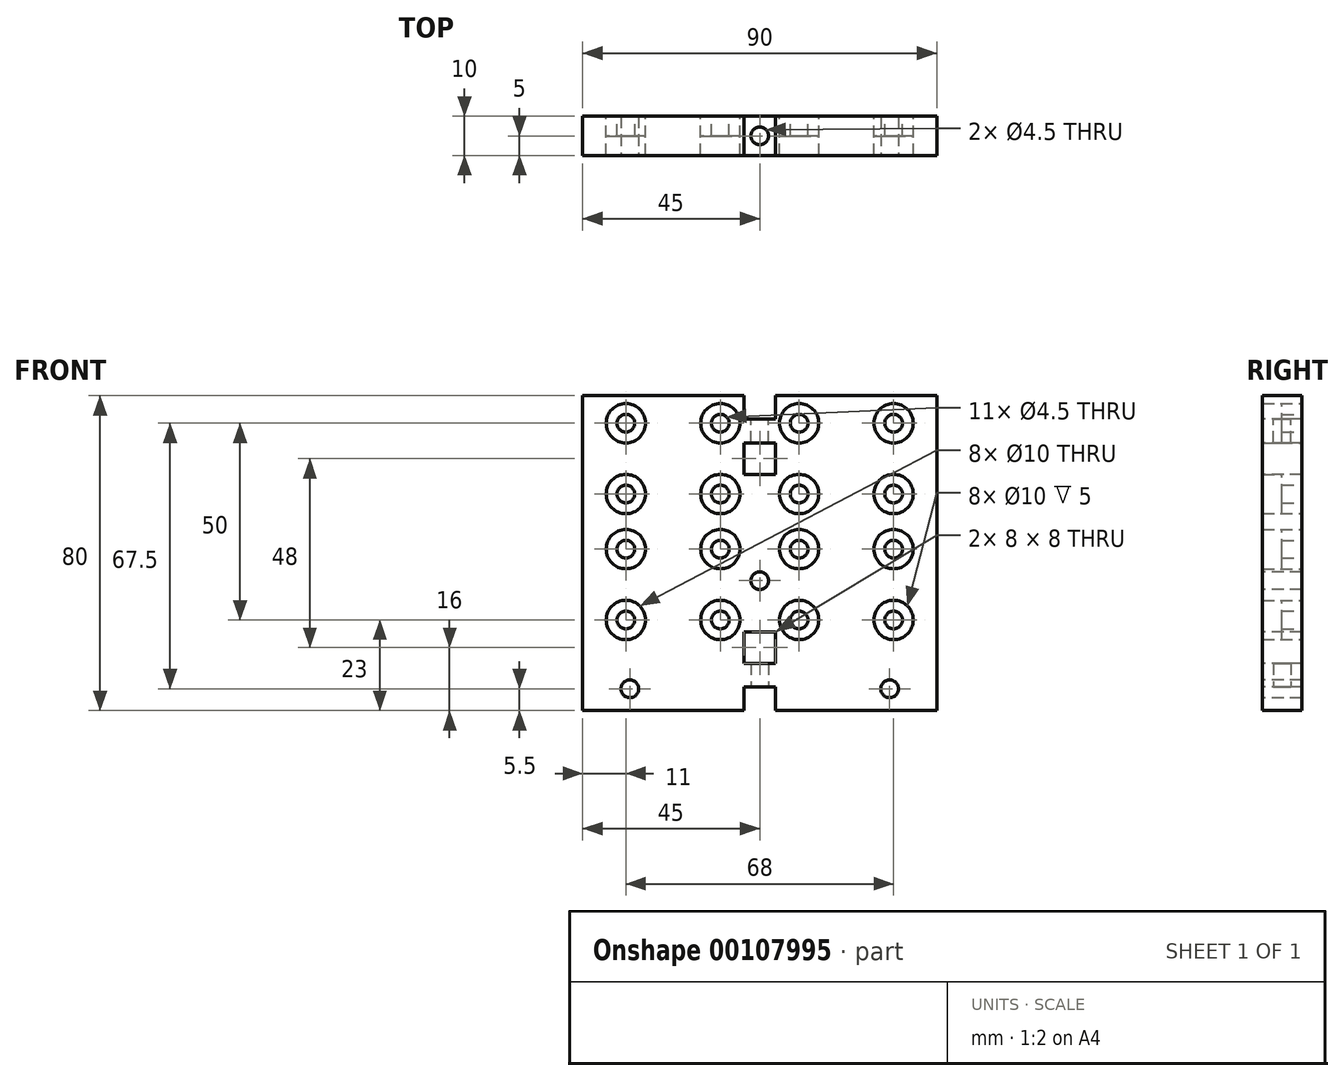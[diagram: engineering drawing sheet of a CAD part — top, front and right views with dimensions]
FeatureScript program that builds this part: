
annotation { "Feature Type Name" : "Feature", "Feature Type Description" : "" }
export const myFeature = defineFeature(function(context is Context, id is Id, definition is map)
    precondition{}
    {
        {
            var Q0;
            Q0=qCreatedBy(makeId("Front.planeOp"),FACE);
            var sketch = newSketch(context, id + "F0", { "sketchPlane" : qUnion([Q0])});
            skLineSegment(sketch, "E0.bottom", {"start": v(0, 0) * mm, "end": v(90, 0) * mm});
            skLineSegment(sketch, "E0.top", {"start": v(0, 80) * mm, "end": v(90, 80) * mm});
            skLineSegment(sketch, "E0.left", {"start": v(0, 0) * mm, "end": v(0, 80) * mm});
            skLineSegment(sketch, "E0.right", {"start": v(90, 0) * mm, "end": v(90, 80) * mm});
            skLineSegment(sketch, "E1.bottom", {"start": v(6, 79) * mm, "end": v(40, 79) * mm});
            skLineSegment(sketch, "E1.top", {"start": v(6, 49) * mm, "end": v(40, 49) * mm});
            skLineSegment(sketch, "E1.left", {"start": v(6, 79) * mm, "end": v(6, 49) * mm});
            skLineSegment(sketch, "E1.right", {"start": v(40, 79) * mm, "end": v(40, 49) * mm});
            skLineSegment(sketch, "E2", {"start": v(45, 80) * mm, "end": v(45, 0) * mm, "construction": true});
            skLineSegment(sketch, "E3", {"start": v(0, 48) * mm, "end": v(90, 48) * mm, "construction": true});
            skCircle(sketch, "E4", {"center": v(11, 73) * mm, "radius": 2.25 * mm});
            skCircle(sketch, "E5", {"center": v(35, 73) * mm, "radius": 2.25 * mm});
            skCircle(sketch, "E6", {"center": v(35, 55) * mm, "radius": 2.25 * mm});
            skCircle(sketch, "E7", {"center": v(11, 55) * mm, "radius": 2.25 * mm});
            skCircle(sketch, "E8.MirrorC", {"center": v(55, 55) * mm, "radius": 2.25 * mm});
            skCircle(sketch, "E9.MirrorC", {"center": v(55, 73) * mm, "radius": 2.25 * mm});
            skCircle(sketch, "E10.MirrorC", {"center": v(79, 55) * mm, "radius": 2.25 * mm});
            skCircle(sketch, "E11.MirrorC", {"center": v(79, 73) * mm, "radius": 2.25 * mm});
            skLineSegment(sketch, "E12.MirrorCS", {"start": v(84, 49) * mm, "end": v(50, 49) * mm});
            skLineSegment(sketch, "E13.MirrorCS", {"start": v(84, 79) * mm, "end": v(50, 79) * mm});
            skLineSegment(sketch, "E14.MirrorCS", {"start": v(84, 79) * mm, "end": v(84, 49) * mm});
            skLineSegment(sketch, "E15.MirrorCS", {"start": v(50, 79) * mm, "end": v(50, 49) * mm});
            skLineSegment(sketch, "E16.MirrorCS", {"start": v(84, 17) * mm, "end": v(84, 47) * mm});
            skLineSegment(sketch, "E17.MirrorCS", {"start": v(84, 47) * mm, "end": v(50, 47) * mm});
            skLineSegment(sketch, "E18.MirrorCS", {"start": v(84, 17) * mm, "end": v(50, 17) * mm});
            skCircle(sketch, "E19.MirrorC", {"center": v(79, 41) * mm, "radius": 2.25 * mm});
            skCircle(sketch, "E20.MirrorC", {"center": v(79, 23) * mm, "radius": 2.25 * mm});
            skCircle(sketch, "E21.MirrorC", {"center": v(55, 23) * mm, "radius": 2.25 * mm});
            skLineSegment(sketch, "E22.MirrorCS", {"start": v(50, 17) * mm, "end": v(50, 47) * mm});
            skCircle(sketch, "E23.MirrorC", {"center": v(55, 41) * mm, "radius": 2.25 * mm});
            skCircle(sketch, "E24.MirrorC", {"center": v(11, 23) * mm, "radius": 2.25 * mm});
            skLineSegment(sketch, "E25.MirrorCS", {"start": v(40, 17) * mm, "end": v(40, 47) * mm});
            skCircle(sketch, "E26.MirrorC", {"center": v(35, 23) * mm, "radius": 2.25 * mm});
            skCircle(sketch, "E27.MirrorC", {"center": v(35, 41) * mm, "radius": 2.25 * mm});
            skLineSegment(sketch, "E28.MirrorCS", {"start": v(6, 17) * mm, "end": v(40, 17) * mm});
            skLineSegment(sketch, "E29.MirrorCS", {"start": v(6, 47) * mm, "end": v(40, 47) * mm});
            skLineSegment(sketch, "E30.MirrorCS", {"start": v(6, 17) * mm, "end": v(6, 47) * mm});
            skCircle(sketch, "E31.MirrorC", {"center": v(11, 41) * mm, "radius": 2.25 * mm});
            skCircle(sketch, "E32", {"center": v(11, 73) * mm, "radius": 5 * mm});
            skCircle(sketch, "E33", {"center": v(11, 55) * mm, "radius": 5 * mm});
            skCircle(sketch, "E34", {"center": v(35, 55) * mm, "radius": 5 * mm});
            skCircle(sketch, "E35", {"center": v(35, 73) * mm, "radius": 5 * mm});
            skCircle(sketch, "E36", {"center": v(55, 73) * mm, "radius": 5 * mm});
            skCircle(sketch, "E37", {"center": v(55, 55) * mm, "radius": 5 * mm});
            skCircle(sketch, "E38", {"center": v(79, 73) * mm, "radius": 5 * mm});
            skCircle(sketch, "E39", {"center": v(79, 55) * mm, "radius": 5 * mm});
            skCircle(sketch, "E40", {"center": v(79, 41) * mm, "radius": 5 * mm});
            skCircle(sketch, "E41", {"center": v(55, 41) * mm, "radius": 5 * mm});
            skCircle(sketch, "E42", {"center": v(35, 41) * mm, "radius": 5 * mm});
            skCircle(sketch, "E43", {"center": v(11, 41) * mm, "radius": 5 * mm});
            skCircle(sketch, "E44", {"center": v(35, 23) * mm, "radius": 5 * mm});
            skCircle(sketch, "E45", {"center": v(11, 23) * mm, "radius": 5 * mm});
            skCircle(sketch, "E46", {"center": v(55, 23) * mm, "radius": 5 * mm});
            skCircle(sketch, "E47", {"center": v(79, 23) * mm, "radius": 5 * mm});
            skSolve(sketch);
        }
        {
            var Q0;
            Q0 = qSketchRegion(id + "F0", true);
            var Q1;
            Q1=makeQuery(id+"F0.imprint","IMPRINT",FACE,{"disambiguationData":[TD([[makeQuery(id+"F0.imprint","IMPRINT",EDGE,{"derivedFrom":sQuery(id+"F0.wireOp",EDGE,"E1.bottom")}),-1.0]])]});
            var Q2;
            Q2=makeQuery(id+"F0.imprint","IMPRINT",FACE,{"disambiguationData":[TD([[makeQuery(id+"F0.imprint","IMPRINT",EDGE,{"derivedFrom":sQuery(id+"F0.wireOp",EDGE,"bZuI6SaU-zsjN-Xk2B-mhtP-13RFlTSP3aNL.bottom")}),-1.0]])]});
            var Q3;
            Q3=makeQuery(id+"F0.imprint","IMPRINT",FACE,{"disambiguationData":[TD([[makeQuery(id+"F0.imprint","IMPRINT",EDGE,{"derivedFrom":sQuery(id+"F0.wireOp",EDGE,"s5ukpUkq-3LvQ-wobc-wGG7-4HGfYjanBSKT.bottom")}),-1.0]])]});
            var Q4;
            Q4=makeQuery(id+"F0.imprint","IMPRINT",FACE,{"disambiguationData":[TD([[makeQuery(id+"F0.imprint","IMPRINT",EDGE,{"derivedFrom":sQuery(id+"F0.wireOp",EDGE,"Jf4Y0yrR-lJhz-zIhG-2X3j-dwFTrGFaGGee.bottom")}),-1.0]])]});
            var Q5;
            Q5=makeQuery(id+"F0.imprint","IMPRINT",FACE,{"disambiguationData":[TD([[makeQuery(id+"F0.imprint","IMPRINT",EDGE,{"derivedFrom":sQuery(id+"F0.wireOp",EDGE,"E12.MirrorCS")}),-1.0]])]});
            var Q6;
            Q6=makeQuery(id+"F0.imprint","IMPRINT",FACE,{"disambiguationData":[TD([[makeQuery(id+"F0.imprint","IMPRINT",EDGE,{"derivedFrom":sQuery(id+"F0.wireOp",EDGE,"E19.MirrorC")}),-1.0]])]});
            var Q7;
            Q7=makeQuery(id+"F0.imprint","IMPRINT",FACE,{"disambiguationData":[TD([[makeQuery(id+"F0.imprint","IMPRINT",EDGE,{"derivedFrom":sQuery(id+"F0.wireOp",EDGE,"E24.MirrorC")}),1.0]])]});
            var Q8;
            Q8=makeQuery(id+"F0.imprint","IMPRINT",FACE,{"disambiguationData":[TD([[makeQuery(id+"F0.imprint","IMPRINT",EDGE,{"derivedFrom":sQuery(id+"F0.wireOp",EDGE,"E4")}),-1.0]])]});
            var Q9;
            Q9=makeQuery(id+"F0.imprint","IMPRINT",FACE,{"disambiguationData":[TD([[makeQuery(id+"F0.imprint","IMPRINT",EDGE,{"derivedFrom":sQuery(id+"F0.wireOp",EDGE,"E5")}),-1.0]])]});
            var Q10;
            Q10=makeQuery(id+"F0.imprint","IMPRINT",FACE,{"disambiguationData":[TD([[makeQuery(id+"F0.imprint","IMPRINT",EDGE,{"derivedFrom":sQuery(id+"F0.wireOp",EDGE,"E9.MirrorC")}),1.0]])]});
            var Q11;
            Q11=makeQuery(id+"F0.imprint","IMPRINT",FACE,{"disambiguationData":[TD([[makeQuery(id+"F0.imprint","IMPRINT",EDGE,{"derivedFrom":sQuery(id+"F0.wireOp",EDGE,"E11.MirrorC")}),1.0]])]});
            var Q12;
            Q12=makeQuery(id+"F0.imprint","IMPRINT",FACE,{"disambiguationData":[TD([[makeQuery(id+"F0.imprint","IMPRINT",EDGE,{"derivedFrom":sQuery(id+"F0.wireOp",EDGE,"E10.MirrorC")}),1.0]])]});
            var Q13;
            Q13=makeQuery(id+"F0.imprint","IMPRINT",FACE,{"disambiguationData":[TD([[makeQuery(id+"F0.imprint","IMPRINT",EDGE,{"derivedFrom":sQuery(id+"F0.wireOp",EDGE,"E8.MirrorC")}),1.0]])]});
            var Q14;
            Q14=makeQuery(id+"F0.imprint","IMPRINT",FACE,{"disambiguationData":[TD([[makeQuery(id+"F0.imprint","IMPRINT",EDGE,{"derivedFrom":sQuery(id+"F0.wireOp",EDGE,"E6")}),-1.0]])]});
            var Q15;
            Q15=makeQuery(id+"F0.imprint","IMPRINT",FACE,{"disambiguationData":[TD([[makeQuery(id+"F0.imprint","IMPRINT",EDGE,{"derivedFrom":sQuery(id+"F0.wireOp",EDGE,"E7")}),-1.0]])]});
            var Q16;
            {var subQ11=sQuery(id+"F0.wireOp",EDGE,"E28.MirrorCS");Q16=makeQuery(id+"F0.imprint","IMPRINT",FACE,{"disambiguationData":[TD([[makeQuery(id+"F0.imprint","IMPRINT",EDGE,{"derivedFrom":subQ11}),1.0]])]});}
            var Q17;
            Q17=makeQuery(id+"F0.imprint","IMPRINT",FACE,{"disambiguationData":[TD([[makeQuery(id+"F0.imprint","IMPRINT",EDGE,{"derivedFrom":sQuery(id+"F0.wireOp",EDGE,"E27.MirrorC")}),1.0]])]});
            var Q18;
            Q18=makeQuery(id+"F0.imprint","IMPRINT",FACE,{"disambiguationData":[TD([[makeQuery(id+"F0.imprint","IMPRINT",EDGE,{"derivedFrom":sQuery(id+"F0.wireOp",EDGE,"E26.MirrorC")}),1.0]])]});
            var Q19;
            Q19=makeQuery(id+"F0.imprint","IMPRINT",FACE,{"disambiguationData":[TD([[makeQuery(id+"F0.imprint","IMPRINT",EDGE,{"derivedFrom":sQuery(id+"F0.wireOp",EDGE,"E31.MirrorC")}),1.0]])]});
            var Q20;
            {var subQ2=sQuery(id+"F0.wireOp",EDGE,"E17.MirrorCS");Q20=makeQuery(id+"F0.imprint","IMPRINT",FACE,{"disambiguationData":[TD([[makeQuery(id+"F0.imprint","IMPRINT",EDGE,{"derivedFrom":subQ2}),1.0]])]});}
            var Q21;
            Q21=makeQuery(id+"F0.imprint","IMPRINT",FACE,{"disambiguationData":[TD([[makeQuery(id+"F0.imprint","IMPRINT",EDGE,{"derivedFrom":sQuery(id+"F0.wireOp",EDGE,"E21.MirrorC")}),-1.0]])]});
            var Q22;
            Q22=makeQuery(id+"F0.imprint","IMPRINT",FACE,{"disambiguationData":[TD([[makeQuery(id+"F0.imprint","IMPRINT",EDGE,{"derivedFrom":sQuery(id+"F0.wireOp",EDGE,"E23.MirrorC")}),-1.0]])]});
            var Q23;
            Q23=makeQuery(id+"F0.imprint","IMPRINT",FACE,{"disambiguationData":[TD([[makeQuery(id+"F0.imprint","IMPRINT",EDGE,{"derivedFrom":sQuery(id+"F0.wireOp",EDGE,"E20.MirrorC")}),-1.0]])]});
            extrude(context, id + "F1", {"entities" : qUnion([Q0, Q1, Q2, Q3, Q4, Q5, Q6, Q7, Q8, Q9, Q10, Q11, Q12, Q13, Q14, Q15, Q16, Q17, Q18, Q19, Q20, Q21, Q22, Q23]), "depth" : 5 * mm});
        }
        {
            var Q0;
            {var subQ2=sQuery(id+"F0.wireOp",EDGE,"E12.MirrorCS");Q0=makeQuery(id+"F0.imprint","IMPRINT",FACE,{"disambiguationData":[TD([[makeQuery(id+"F0.imprint","IMPRINT",EDGE,{"derivedFrom":subQ2}),-1.0]])]});}
            var Q1;
            {var subQ2=sQuery(id+"F0.wireOp",EDGE,"E17.MirrorCS");Q1=makeQuery(id+"F0.imprint","IMPRINT",FACE,{"disambiguationData":[TD([[makeQuery(id+"F0.imprint","IMPRINT",EDGE,{"derivedFrom":subQ2}),1.0]])]});}
            var Q2;
            {var subQ11=sQuery(id+"F0.wireOp",EDGE,"E28.MirrorCS");Q2=makeQuery(id+"F0.imprint","IMPRINT",FACE,{"disambiguationData":[TD([[makeQuery(id+"F0.imprint","IMPRINT",EDGE,{"derivedFrom":subQ11}),1.0]])]});}
            var Q3;
            {var subQ6=sQuery(id+"F0.wireOp",EDGE,"E1.bottom");Q3=makeQuery(id+"F0.imprint","IMPRINT",FACE,{"disambiguationData":[TD([[makeQuery(id+"F0.imprint","IMPRINT",EDGE,{"derivedFrom":subQ6}),-1.0]])]});}
            var Q4;
            Q4=makeQuery(id+"F0.imprint","IMPRINT",FACE,{"disambiguationData":[TD([[makeQuery(id+"F0.imprint","IMPRINT",EDGE,{"derivedFrom":sQuery(id+"F0.wireOp",EDGE,"E0.bottom")}),1.0]])]});
            extrude(context, id + "F2", {"entities" : qUnion([Q0, Q1, Q2, Q3, Q4]), "operationType" : NewBodyOperationType.ADD, "depth" : 10 * mm});
        }
        {
            var Q0;
            Q0=makeQuery(id+"F2.opExtrude","CAP_FACE",FACE,{"disambiguationData":[OSD([sQuery(id+"F0.wireOp",EDGE,"E0.bottom"),sQuery(id+"F0.wireOp",EDGE,"E0.top"),sQuery(id+"F0.wireOp",EDGE,"E0.left"),sQuery(id+"F0.wireOp",EDGE,"E0.right"),sQuery(id+"F0.wireOp",EDGE,"E1.bottom"),sQuery(id+"F0.wireOp",EDGE,"E1.top"),sQuery(id+"F0.wireOp",EDGE,"E1.left"),sQuery(id+"F0.wireOp",EDGE,"E1.right"),sQuery(id+"F0.wireOp",EDGE,"E12.MirrorCS"),sQuery(id+"F0.wireOp",EDGE,"E13.MirrorCS"),sQuery(id+"F0.wireOp",EDGE,"E15.MirrorCS"),sQuery(id+"F0.wireOp",EDGE,"E14.MirrorCS"),sQuery(id+"F0.wireOp",EDGE,"E17.MirrorCS"),sQuery(id+"F0.wireOp",EDGE,"E16.MirrorCS"),sQuery(id+"F0.wireOp",EDGE,"E22.MirrorCS"),sQuery(id+"F0.wireOp",EDGE,"E18.MirrorCS"),sQuery(id+"F0.wireOp",EDGE,"E25.MirrorCS"),sQuery(id+"F0.wireOp",EDGE,"E28.MirrorCS"),sQuery(id+"F0.wireOp",EDGE,"E29.MirrorCS"),sQuery(id+"F0.wireOp",EDGE,"E30.MirrorCS")])],"isStart":false});
            var sketch = newSketch(context, id + "F3", { "sketchPlane" : qUnion([Q0])});
            skLineSegment(sketch, "E48.bottom", {"start": v(41, 60) * mm, "end": v(49, 60) * mm});
            skLineSegment(sketch, "E48.top", {"start": v(41, 68) * mm, "end": v(49, 68) * mm});
            skLineSegment(sketch, "E48.left", {"start": v(41, 68) * mm, "end": v(41, 60) * mm});
            skLineSegment(sketch, "E48.right", {"start": v(49, 68) * mm, "end": v(49, 60) * mm});
            skLineSegment(sketch, "E49.bottom", {"start": v(41, 80) * mm, "end": v(49, 80) * mm});
            skLineSegment(sketch, "E49.top", {"start": v(41, 74) * mm, "end": v(49, 74) * mm});
            skLineSegment(sketch, "E49.left", {"start": v(41, 80) * mm, "end": v(41, 74) * mm});
            skLineSegment(sketch, "E49.right", {"start": v(49, 80) * mm, "end": v(49, 74) * mm});
            skLineSegment(sketch, "E50", {"start": v(0, 40) * mm, "end": v(90, 40) * mm, "construction": true});
            skLineSegment(sketch, "E51.MirrorCS", {"start": v(41, 0) * mm, "end": v(49, 0) * mm});
            skLineSegment(sketch, "E52.MirrorCS", {"start": v(41, 6) * mm, "end": v(49, 6) * mm});
            skLineSegment(sketch, "E53.MirrorCS", {"start": v(41, 20) * mm, "end": v(49, 20) * mm});
            skLineSegment(sketch, "E54.MirrorCS", {"start": v(49, 0) * mm, "end": v(49, 6) * mm});
            skLineSegment(sketch, "E55.MirrorCS", {"start": v(41, 0) * mm, "end": v(41, 6) * mm});
            skLineSegment(sketch, "E56.MirrorCS", {"start": v(41, 12) * mm, "end": v(41, 20) * mm});
            skLineSegment(sketch, "E57.MirrorCS", {"start": v(49, 12) * mm, "end": v(49, 20) * mm});
            skLineSegment(sketch, "E58.MirrorCS", {"start": v(41, 12) * mm, "end": v(49, 12) * mm});
            skSolve(sketch);
        }
        {
            var Q0;
            Q0=makeQuery(id+"F3.imprint","IMPRINT",FACE,{"disambiguationData":[TD([[makeQuery(id+"F3.imprint","IMPRINT",EDGE,{"derivedFrom":sQuery(id+"F3.wireOp",EDGE,"E48.bottom")}),1.0]])]});
            var Q1;
            Q1=makeQuery(id+"F3.imprint","IMPRINT",FACE,{"disambiguationData":[TD([[makeQuery(id+"F3.imprint","IMPRINT",EDGE,{"derivedFrom":sQuery(id+"F3.wireOp",EDGE,"E49.bottom")}),-1.0]])]});
            var Q2;
            Q2=makeQuery(id+"F3.imprint","IMPRINT",FACE,{"disambiguationData":[TD([[makeQuery(id+"F3.imprint","IMPRINT",EDGE,{"derivedFrom":sQuery(id+"F3.wireOp",EDGE,"E53.MirrorCS")}),-1.0]])]});
            var Q3;
            Q3=makeQuery(id+"F3.imprint","IMPRINT",FACE,{"disambiguationData":[TD([[makeQuery(id+"F3.imprint","IMPRINT",EDGE,{"derivedFrom":sQuery(id+"F3.wireOp",EDGE,"E51.MirrorCS")}),1.0]])]});
            extrude(context, id + "F4", {"entities" : qUnion([Q0, Q1, Q2, Q3]), "operationType" : NewBodyOperationType.REMOVE, "endBound" : BoundingType.THROUGH_ALL, "oppositeDirection" : true, "depth" : 25 * mm});
        }
        {
            var Q0;
            {var subQ0=sQuery(id+"F0.wireOp",EDGE,"E0.top");Q0=makeQuery(id+"F2.boolean.opBoolean","MERGE",FACE,{"derivedFrom":[makeQuery(id+"F1.opExtrude","SWEPT_FACE",FACE,{"disambiguationData":[OSD([subQ0])]}),makeQuery(id+"F2.opExtrude","SWEPT_FACE",FACE,{"disambiguationData":[OSD([subQ0])]})]});}
            var sketch = newSketch(context, id + "F5", { "sketchPlane" : qUnion([Q0])});
            skLineSegment(sketch, "E59.bottom", {"start": v(41, 0) * mm, "end": v(49, 0) * mm});
            skLineSegment(sketch, "E59.top", {"start": v(41, -10) * mm, "end": v(49, -10) * mm});
            skLineSegment(sketch, "E59.left", {"start": v(41, 0) * mm, "end": v(41, -10) * mm});
            skLineSegment(sketch, "E59.right", {"start": v(49, 0) * mm, "end": v(49, -10) * mm});
            skLineSegment(sketch, "E60", {"start": v(45, 0) * mm, "end": v(45, -10) * mm, "construction": true});
            skLineSegment(sketch, "E61", {"start": v(41, -5) * mm, "end": v(49, -5) * mm, "construction": true});
            skCircle(sketch, "E62", {"center": v(45, -5) * mm, "radius": 2.25 * mm});
            skSolve(sketch);
        }
        {
            var Q0;
            Q0=makeQuery(id+"F5.imprint","IMPRINT",FACE,{"disambiguationData":[TD([[makeQuery(id+"F5.imprint","IMPRINT",EDGE,{"derivedFrom":sQuery(id+"F5.wireOp",EDGE,"E62")}),1.0]])]});
            extrude(context, id + "F6", {"entities" : qUnion([Q0]), "operationType" : NewBodyOperationType.REMOVE, "oppositeDirection" : true, "depth" : 20 * mm});
        }
        {
            var Q0;
            {var subQ1=sQuery(id+"F0.wireOp",EDGE,"E0.left");var subQ3=sQuery(id+"F0.wireOp",EDGE,"E0.bottom");Q0=makeQuery(id+"F4.boolean.opBoolean","SPLIT",FACE,{"disambiguationData":[TD([makeQuery(id+"F1.opExtrude","SWEPT_FACE",FACE,{"disambiguationData":[OSD([subQ1])]})])],"derivedFrom":makeQuery(id+"F2.boolean.opBoolean","MERGE",FACE,{"derivedFrom":[makeQuery(id+"F1.opExtrude","SWEPT_FACE",FACE,{"disambiguationData":[OSD([subQ3])]}),makeQuery(id+"F2.opExtrude","SWEPT_FACE",FACE,{"disambiguationData":[OSD([subQ3])]})]})});}
            var sketch = newSketch(context, id + "F7", { "sketchPlane" : qUnion([Q0])});
            skLineSegment(sketch, "E63.bottom", {"start": v(41, 10) * mm, "end": v(49, 10) * mm, "construction": true});
            skLineSegment(sketch, "E63.top", {"start": v(41, 0) * mm, "end": v(49, 0) * mm, "construction": true});
            skLineSegment(sketch, "E63.left", {"start": v(41, 10) * mm, "end": v(41, 0) * mm, "construction": true});
            skLineSegment(sketch, "E63.right", {"start": v(49, 10) * mm, "end": v(49, 0) * mm, "construction": true});
            skLineSegment(sketch, "E64", {"start": v(41, 10) * mm, "end": v(49, 0) * mm, "construction": true});
            skLineSegment(sketch, "E65", {"start": v(41, 0) * mm, "end": v(49, 10) * mm, "construction": true});
            skCircle(sketch, "E66", {"center": v(45, 5) * mm, "radius": 2.25 * mm});
            skSolve(sketch);
        }
        {
            var Q0;
            Q0=makeQuery(id+"F7.imprint","IMPRINT",FACE,{"disambiguationData":[TD([[makeQuery(id+"F7.imprint","IMPRINT",EDGE,{"derivedFrom":sQuery(id+"F7.wireOp",EDGE,"E66")}),1.0]])]});
            extrude(context, id + "F8", {"entities" : qUnion([Q0]), "operationType" : NewBodyOperationType.REMOVE, "oppositeDirection" : true, "depth" : 20 * mm});
        }
        {
            var Q0;
            Q0=makeQuery(id+"F2.opExtrude","CAP_FACE",FACE,{"disambiguationData":[OSD([sQuery(id+"F0.wireOp",EDGE,"E0.bottom"),sQuery(id+"F0.wireOp",EDGE,"E0.top"),sQuery(id+"F0.wireOp",EDGE,"E0.left"),sQuery(id+"F0.wireOp",EDGE,"E0.right"),sQuery(id+"F0.wireOp",EDGE,"E32"),sQuery(id+"F0.wireOp",EDGE,"E33"),sQuery(id+"F0.wireOp",EDGE,"E34"),sQuery(id+"F0.wireOp",EDGE,"E35"),sQuery(id+"F0.wireOp",EDGE,"E36"),sQuery(id+"F0.wireOp",EDGE,"E37"),sQuery(id+"F0.wireOp",EDGE,"E38"),sQuery(id+"F0.wireOp",EDGE,"E39"),sQuery(id+"F0.wireOp",EDGE,"E40"),sQuery(id+"F0.wireOp",EDGE,"E41"),sQuery(id+"F0.wireOp",EDGE,"E42"),sQuery(id+"F0.wireOp",EDGE,"E43"),sQuery(id+"F0.wireOp",EDGE,"E44"),sQuery(id+"F0.wireOp",EDGE,"E45"),sQuery(id+"F0.wireOp",EDGE,"E46"),sQuery(id+"F0.wireOp",EDGE,"E47")])],"isStart":false});
            var sketch = newSketch(context, id + "F9", { "sketchPlane" : qUnion([Q0])});
            skLineSegment(sketch, "E67", {"start": v(45, 74) * mm, "end": v(45, 6) * mm, "construction": true});
            skCircle(sketch, "E68", {"center": v(45, 33) * mm, "radius": 2.25 * mm});
            skCircle(sketch, "E69", {"center": v(12, 5.5) * mm, "radius": 2.25 * mm});
            skCircle(sketch, "E70", {"center": v(78, 5.5) * mm, "radius": 2.25 * mm});
            skSolve(sketch);
        }
        {
            var Q0;
            Q0=makeQuery(id+"F9.imprint","IMPRINT",FACE,{"disambiguationData":[TD([[makeQuery(id+"F9.imprint","IMPRINT",EDGE,{"derivedFrom":sQuery(id+"F9.wireOp",EDGE,"E68")}),1.0]])]});
            var Q1;
            Q1=makeQuery(id+"F9.imprint","IMPRINT",FACE,{"disambiguationData":[TD([[makeQuery(id+"F9.imprint","IMPRINT",EDGE,{"derivedFrom":sQuery(id+"F9.wireOp",EDGE,"E69")}),1.0]])]});
            var Q2;
            Q2=makeQuery(id+"F9.imprint","IMPRINT",FACE,{"disambiguationData":[TD([[makeQuery(id+"F9.imprint","IMPRINT",EDGE,{"derivedFrom":sQuery(id+"F9.wireOp",EDGE,"E70")}),1.0]])]});
            extrude(context, id + "F10", {"entities" : qUnion([Q0, Q1, Q2]), "operationType" : NewBodyOperationType.REMOVE, "endBound" : BoundingType.THROUGH_ALL, "oppositeDirection" : true, "depth" : 25 * mm});
        }
    });
